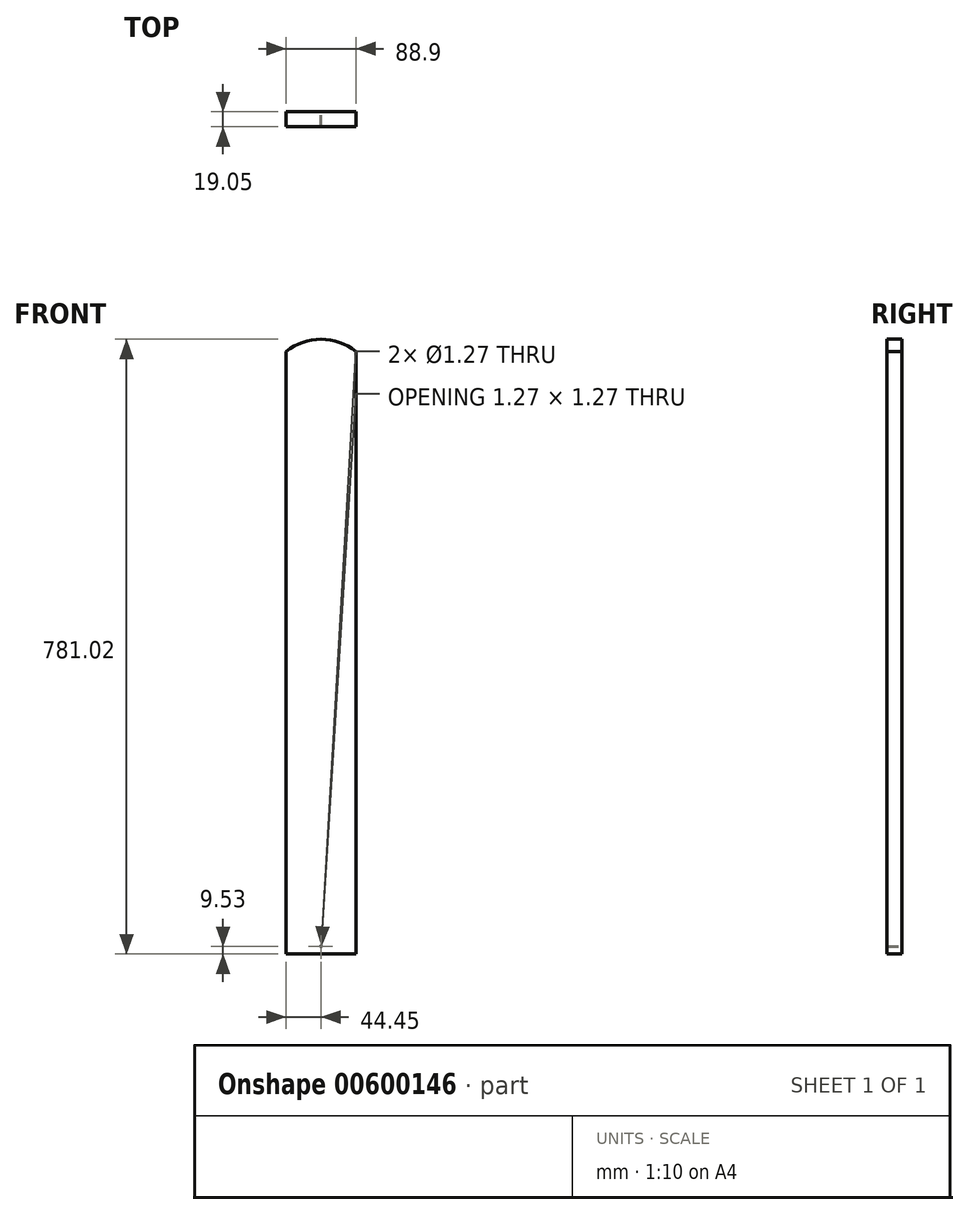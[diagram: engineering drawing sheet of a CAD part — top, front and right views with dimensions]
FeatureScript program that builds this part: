
annotation { "Feature Type Name" : "Feature", "Feature Type Description" : "" }
export const myFeature = defineFeature(function(context is Context, id is Id, definition is map)
    precondition{}
    {
        {
            var Q0;
            Q0=qCreatedBy(makeId("Front.planeOp"),FACE);
            var sketch = newSketch(context, id + "F0", { "sketchPlane" : qUnion([Q0])});
            skLineSegment(sketch, "E0.top", {"start": v(-44.45, -390.53) * mm, "end": v(44.45, -390.53) * mm});
            skLineSegment(sketch, "E0.left", {"start": v(-44.45, 374.65) * mm, "end": v(-44.45, -390.53) * mm});
            skLineSegment(sketch, "E0.right", {"start": v(44.45, 374.65) * mm, "end": v(44.45, -390.53) * mm});
            skLineSegment(sketch, "E1", {"start": v(-44.45, 390.52) * mm, "end": v(44.45, -390.53) * mm, "construction": true});
            skArc(sketch, "E2", {"start": v(44.45, 374.65) * mm, "mid": v(0, 390.5) * mm, "end": v(-44.45, 374.65) * mm});
            skSolve(sketch);
        }
        {
            var Q0;
            Q0 = qSketchRegion(id + "F0", true);
            extrude(context, id + "F1", {"entities" : qUnion([Q0]), "depth" : 19.05 * mm, "offsetDistance" : 25.4 * mm});
        }
        {
            var Q0;
            Q0=makeQuery(id+"F1.opExtrude","CAP_FACE",FACE,{"disambiguationData":[OSD([sQuery(id+"F0.wireOp",EDGE,"E0.top"),sQuery(id+"F0.wireOp",EDGE,"E0.left"),sQuery(id+"F0.wireOp",EDGE,"E0.right"),sQuery(id+"F0.wireOp",EDGE,"E2")])],"isStart":true});
            var sketch = newSketch(context, id + "F2", { "sketchPlane" : qUnion([Q0])});
            skLineSegment(sketch, "E3", {"start": v(44.45, -390.53) * mm, "end": v(-44.45, -390.53) * mm});
            skCircle(sketch, "E4", {"center": v(0, -381) * mm, "radius": 0.64 * mm});
            skSolve(sketch);
        }
        {
            var Q0;
            Q0 = qSketchRegion(id + "F2", true);
            extrude(context, id + "F3", {"entities" : qUnion([Q0]), "operationType" : NewBodyOperationType.REMOVE, "endBound" : BoundingType.THROUGH_ALL, "oppositeDirection" : true, "depth" : 25.4 * mm, "offsetDistance" : 25.4 * mm});
        }
    });
